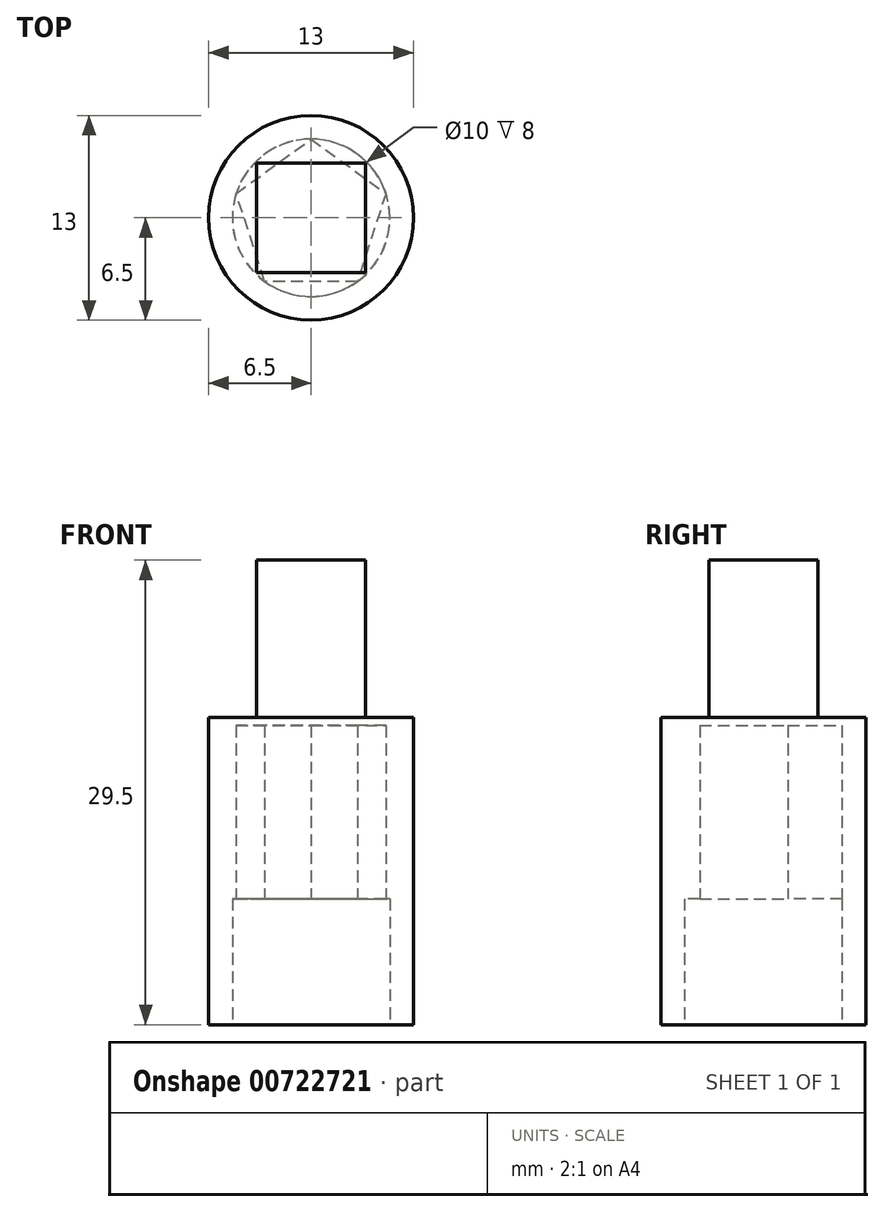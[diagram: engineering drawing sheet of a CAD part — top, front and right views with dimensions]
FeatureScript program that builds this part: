
annotation { "Feature Type Name" : "Feature", "Feature Type Description" : "" }
export const myFeature = defineFeature(function(context is Context, id is Id, definition is map)
    precondition{}
    {
        {
            var Q0;
            Q0=qCreatedBy(makeId("Top.planeOp"),FACE);
            var sketch = newSketch(context, id + "F0", { "sketchPlane" : qUnion([Q0])});
            skCircle(sketch, "E0", {"center": v(0, 0) * mm, "radius": 5 * mm});
            skCircle(sketch, "E1", {"center": v(0, 0) * mm, "radius": 6.5 * mm});
            skSolve(sketch);
        }
        {
            var Q0;
            Q0=makeQuery(id+"F0.imprint","IMPRINT",FACE,{"disambiguationData":[TD([[makeQuery(id+"F0.imprint","IMPRINT",EDGE,{"derivedFrom":sQuery(id+"F0.wireOp",EDGE,"E0")}),-1.0]])]});
            extrude(context, id + "F1", {"entities" : qUnion([Q0]), "depth" : 8 * mm, "offsetDistance" : 25 * mm});
        }
        {
            var Q0;
            Q0=makeQuery(id+"F1.opExtrude","CAP_FACE",FACE,{"disambiguationData":[OSD([sQuery(id+"F0.wireOp",EDGE,"E0"),sQuery(id+"F0.wireOp",EDGE,"E1")])],"isStart":false});
            var sketch = newSketch(context, id + "F2", { "sketchPlane" : qUnion([Q0])});
            skCircle(sketch, "E2.cCircle", {"center": v(0, 0) * mm, "radius": 5 * mm, "construction": true});
            skLineSegment(sketch, "E2.0", {"start": v(2.94, -4.05) * mm, "end": v(-2.94, -4.05) * mm});
            skLineSegment(sketch, "E2.1", {"start": v(-2.94, -4.05) * mm, "end": v(-4.76, 1.55) * mm});
            skLineSegment(sketch, "E2.2", {"start": v(-4.76, 1.55) * mm, "end": v(0, 5) * mm});
            skLineSegment(sketch, "E2.3", {"start": v(0, 5) * mm, "end": v(4.76, 1.55) * mm});
            skLineSegment(sketch, "E2.4", {"start": v(4.76, 1.55) * mm, "end": v(2.94, -4.05) * mm});
            skCircle(sketch, "E3", {"center": v(0, 0) * mm, "radius": 6.5 * mm});
            skSolve(sketch);
        }
        {
            var Q0;
            Q0 = qSketchRegion(id + "F2", true);
            extrude(context, id + "F3", {"entities" : qUnion([Q0]), "operationType" : NewBodyOperationType.ADD, "depth" : 11 * mm, "offsetDistance" : 25 * mm});
        }
        {
            var Q0;
            Q0=makeQuery(id+"F3.opExtrude","CAP_FACE",FACE,{"disambiguationData":[OSD([sQuery(id+"F2.wireOp",EDGE,"E2.0"),sQuery(id+"F2.wireOp",EDGE,"E2.1"),sQuery(id+"F2.wireOp",EDGE,"E2.2"),sQuery(id+"F2.wireOp",EDGE,"E2.3"),sQuery(id+"F2.wireOp",EDGE,"E2.4"),sQuery(id+"F2.wireOp",EDGE,"E3")])],"isStart":false});
            var sketch = newSketch(context, id + "F4", { "sketchPlane" : qUnion([Q0])});
            skCircle(sketch, "E4", {"center": v(0, 0) * mm, "radius": 6.5 * mm});
            skSolve(sketch);
        }
        {
            var Q0;
            Q0 = qSketchRegion(id + "F4", true);
            extrude(context, id + "F5", {"entities" : qUnion([Q0]), "operationType" : NewBodyOperationType.ADD, "depth" : 0.5 * mm, "offsetDistance" : 25 * mm});
        }
        {
            var Q0;
            Q0=makeQuery(id+"F5.opExtrude","CAP_FACE",FACE,{"disambiguationData":[OSD([sQuery(id+"F4.wireOp",EDGE,"E4")])],"isStart":false});
            var sketch = newSketch(context, id + "F6", { "sketchPlane" : qUnion([Q0])});
            skCircle(sketch, "E5", {"center": v(0, 0) * mm, "radius": 4.9 * mm, "construction": true});
            skLineSegment(sketch, "E6.0", {"start": v(3.46, -3.46) * mm, "end": v(-3.46, -3.46) * mm});
            skLineSegment(sketch, "E6.1", {"start": v(-3.46, -3.46) * mm, "end": v(-3.46, 3.46) * mm});
            skLineSegment(sketch, "E6.2", {"start": v(-3.46, 3.46) * mm, "end": v(3.46, 3.46) * mm});
            skLineSegment(sketch, "E6.3", {"start": v(3.46, 3.46) * mm, "end": v(3.46, -3.46) * mm});
            skSolve(sketch);
        }
        {
            var Q0;
            Q0 = qSketchRegion(id + "F6", true);
            extrude(context, id + "F7", {"entities" : qUnion([Q0]), "operationType" : NewBodyOperationType.ADD, "depth" : 10 * mm, "offsetDistance" : 25 * mm});
        }
    });
